# Revit family: PRD_FrankeWS_Prss-actnSlf-clsngPllrTps_AQUALINE-SExtensionAdapter_ZAQUA002
name_source: partatom
category: Specialty Equipment
revit_build: Autodesk Revit 2018 (Build: 20190510_1515(x64)
units: mm (PartAtom-declared; Revit-internal decimal feet)

## family parameters
Always vertical = No
Cut with Voids When Loaded = No
OmniClass Number = 23.45.55.11
OmniClass Title = Sanitary Components
Part Type = Normal
Room Calculation Point = No
Round Connector Dimension = Use Diameter
Shared = No
Work Plane-Based = Yes

## types (1)
- ZAQUA002
    AssetType = Fixed
    BIMObjectName = PRD_AR_Press-actionSelf-closingPillarTaps_AQUALINE-SExtensionAdapter_ZAQUA002
    BodyMaterial = PRD_AR_ChromatedBrass_HighPolished
    Category = Pr_40_20_87_66, Press-action self-closing pillar taps
    Default Elevation = 1219 mm
    Description = Extension adapter for AQUALINE-S self-closing bib tap, stackable (30 mm).
    DurationUnit = year
    FaucetType = USERDEFINED
    Features = Extension adapter
    GrossWeight = 0.32 kg
    IfcExportAs = IfcValveType
    IfcExportType = FAUCET
    Manufacturer = KWC Group AG
    ManufacturerName = KWC Group AG
    ManufacturerURL = www.kwc.com
    Model = ZAQUA002
    ModelNumber = 2000101433
    ModelReference = ZAQUA002
    NBSDescription = Taps and water supply fittings for washbasins and troughs
    NBSReference = 45-35-70/371
    Name = AQUALINE-S Extension adapter ZAQUA002
    NetWeight = 0.29 kg
    NominalDepth = 0 mm  [stored 0 ft]
    NominalHeight = 0 mm  [stored 0 ft]
    NominalWidth = 0 mm  [stored 0 ft]
    ProductInformation = https://pim.kwc.com
    TypeOfExtension = For bib taps
    URL = www.kwc.com
    Uniclass2015Code = Pr_40_20_87_66
    Uniclass2015Title = Press-action self-closing pillar taps
    Uniclass2015Version = Products v1.23
    Version = 1
    WarrantyDurationUnit = year

note: [stored X ft] marks values corroborated as IEEE doubles in the binary element streams (Revit-internal decimal feet)

## geometry (parser evidence)
native form markers: Sweep x3
no freeform markers — native parametric forms only
